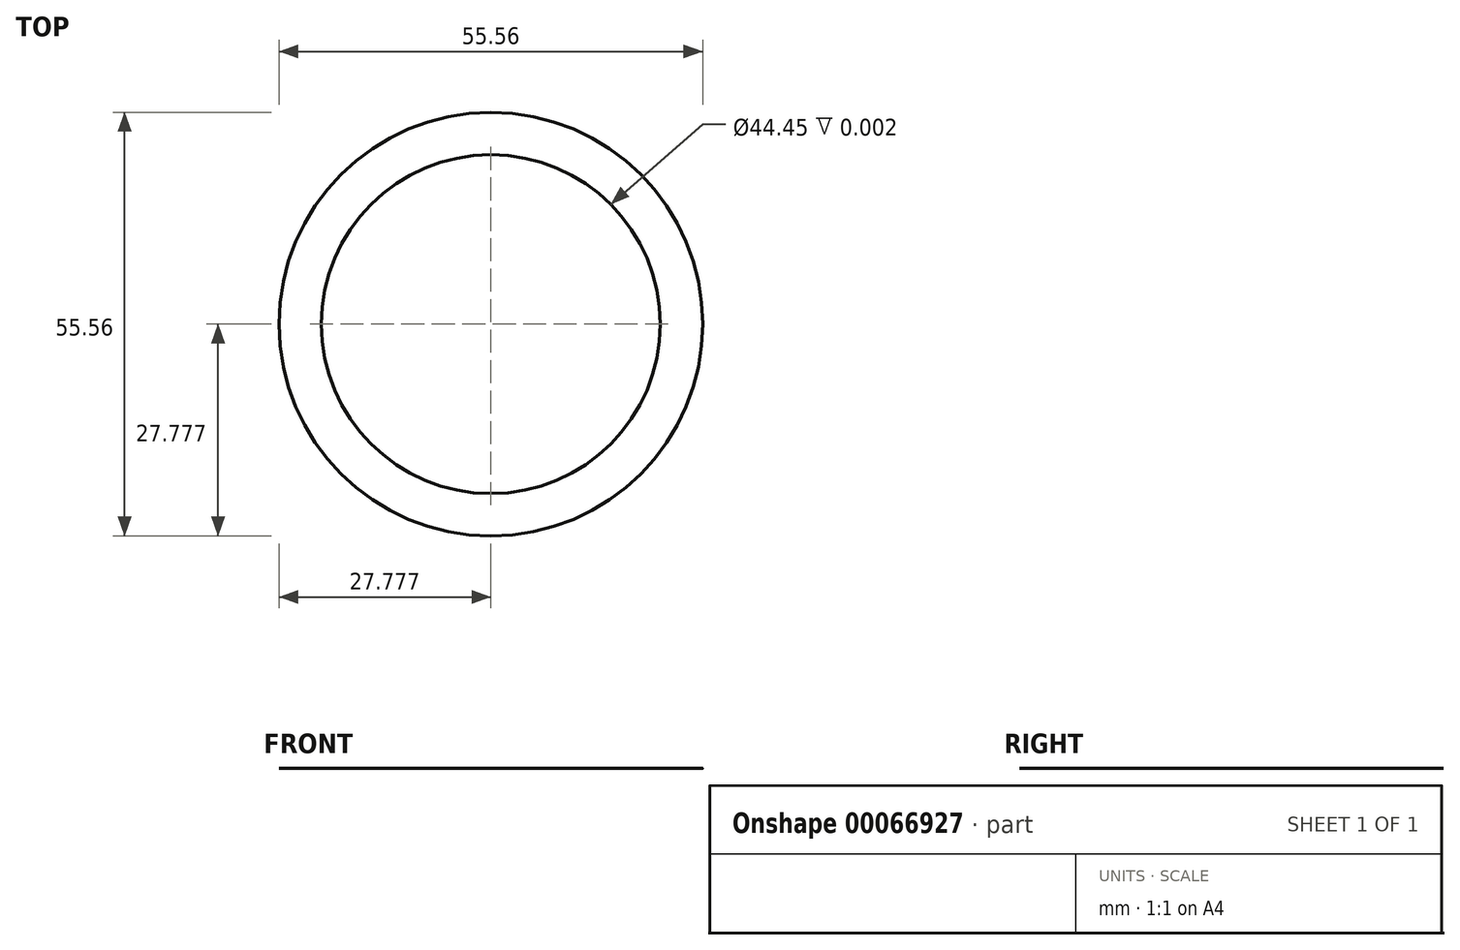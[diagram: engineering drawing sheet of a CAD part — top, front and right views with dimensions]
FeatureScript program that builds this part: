
annotation { "Feature Type Name" : "Feature", "Feature Type Description" : "" }
export const myFeature = defineFeature(function(context is Context, id is Id, definition is map)
    precondition{}
    {
        {
            var Q0;
            Q0=qCreatedBy(makeId("Top.planeOp"),FACE);
            var sketch = newSketch(context, id + "F0", { "sketchPlane" : qUnion([Q0])});
            skCircle(sketch, "E0", {"center": v(-46, -16.1) * mm, "radius": 27.78 * mm});
            skSolve(sketch);
        }
        {
            var Q0;
            Q0=makeQuery(id+"F0.imprint","IMPRINT",FACE,{"disambiguationData":[TD([[makeQuery(id+"F0.imprint","IMPRINT",EDGE,{"derivedFrom":sQuery(id+"F0.wireOp",EDGE,"E0")}),1.0]])]});
            extrude(context, id + "F1", {"entities" : qUnion([Q0]), "depth" : 1 / 406.4 * mm});
        }
        {
            var Q0;
            Q0=makeQuery(id+"F1.opExtrude","CAP_FACE",FACE,{"disambiguationData":[OSD([sQuery(id+"F0.wireOp",EDGE,"E0")])],"isStart":true});
            var sketch = newSketch(context, id + "F2", { "sketchPlane" : qUnion([Q0])});
            skCircle(sketch, "E1", {"center": v(-46, 16.1) * mm, "radius": 22.23 * mm});
            skSolve(sketch);
        }
        {
            var Q0;
            Q0 = qSketchRegion(id + "F2", true);
            extrude(context, id + "F3", {"entities" : qUnion([Q0]), "operationType" : NewBodyOperationType.REMOVE, "oppositeDirection" : true, "depth" : 25.4 * mm});
        }
    });
